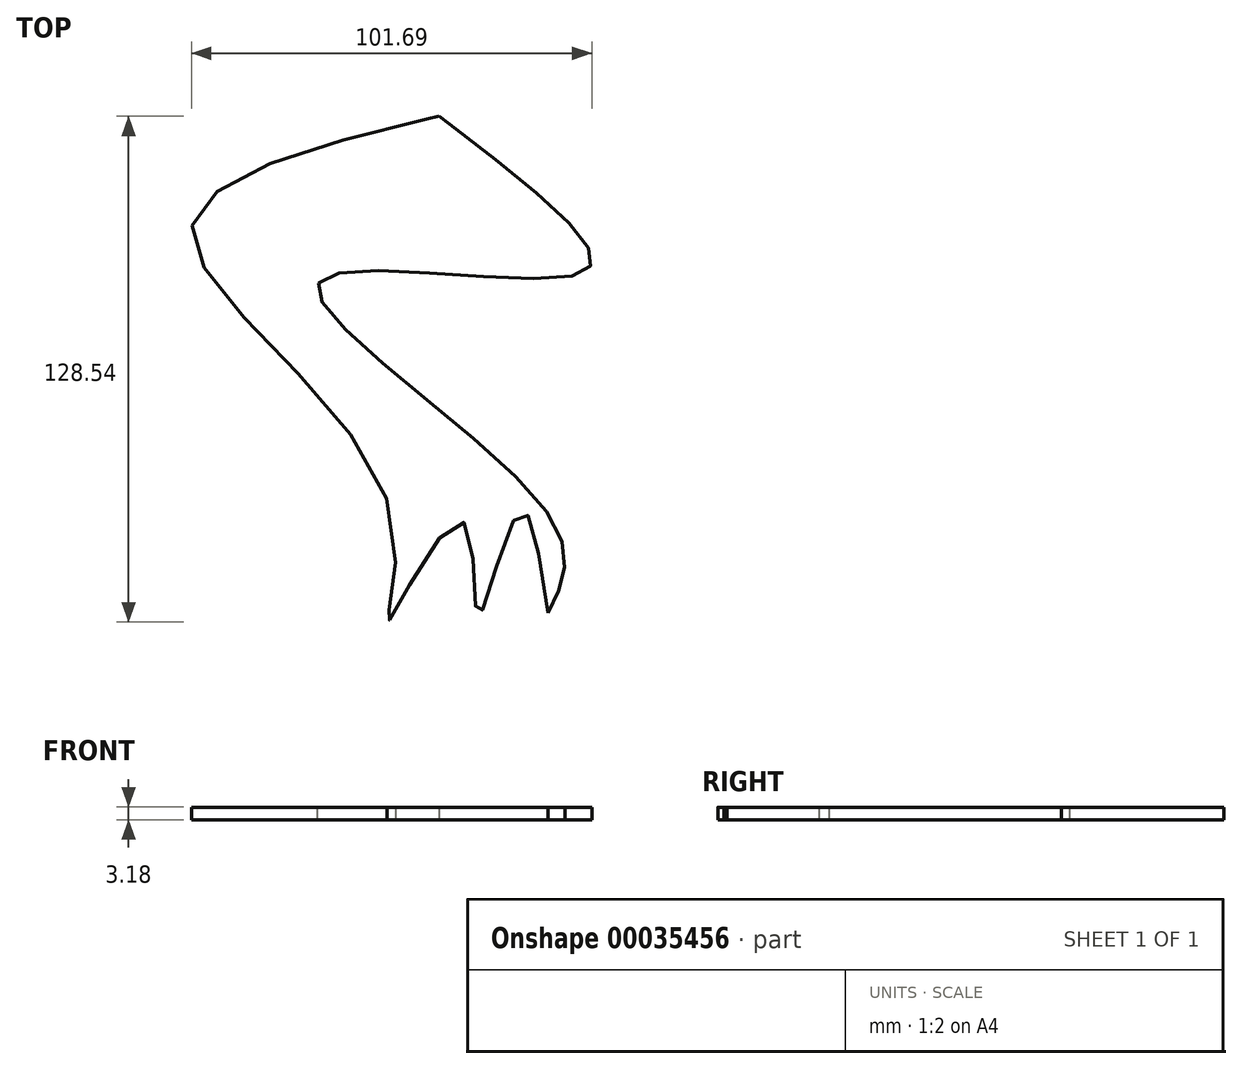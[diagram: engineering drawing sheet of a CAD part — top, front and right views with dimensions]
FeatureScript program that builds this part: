
annotation { "Feature Type Name" : "Feature", "Feature Type Description" : "" }
export const myFeature = defineFeature(function(context is Context, id is Id, definition is map)
    precondition{}
    {
        {
            var Q0;
            Q0=qCreatedBy(makeId("Top.planeOp"),FACE);
            var sketch = newSketch(context, id + "F0", { "sketchPlane" : qUnion([Q0])});
            skLineSegment(sketch, "E0", {"start": v(0, 123.85) * mm, "end": v(0, -125.19) * mm, "construction": true});
            skPoint(sketch, "E1.orphan", {"position": v(0, -125.19) * mm});
            skPoint(sketch, "E2.MirrorCS.end.orphan", {"position": v(0, 123.85) * mm});
            skFitSpline(sketch, "E3.MirrorCS", {"points": [v(-53.72, -66.97) * mm, v(-116.54, -97.18) * mm, v(-66.43, -165.92) * mm, v(-66.43, -195.15) * mm, v(-47.8, -169.87) * mm, v(-43.85, -193.97) * mm, v(-33.58, -167.9) * mm, v(-26.07, -193.18) * mm], "startDerivative": vector(-503.65, -120.96) * mm, "endDerivative": vector(51.87, -371.98) * mm});
            skFitSpline(sketch, "E4.MirrorCS", {"points": [v(-26.07, -193.18) * mm, v(-26.07, -167.9) * mm, v(-84.18, -109.1) * mm, v(-17.07, -106.69) * mm, v(-53.72, -66.97) * mm], "startDerivative": vector(66.51, 128.57) * mm, "endDerivative": vector(-279.5, 211.68) * mm});
            skFitSpline(sketch, "E5.MirrorCS", {"points": [v(-53.72, -66.97) * mm, v(-116.54, -97.18) * mm, v(-66.43, -165.92) * mm, v(-66.43, -195.15) * mm, v(-47.8, -169.87) * mm, v(-43.85, -193.97) * mm, v(-33.58, -167.9) * mm, v(-26.07, -193.18) * mm], "startDerivative": vector(-503.65, -120.96) * mm, "endDerivative": vector(51.87, -371.98) * mm});
            skArc(sketch, "E6.MirrorCS", {"start": v(-56.92, -67.74) * mm, "mid": v(-53.87, -67.7) * mm, "end": v(-51.1, -68.96) * mm});
            skSolve(sketch);
        }
        {
            var Q0;
            Q0=makeQuery(id+"F0.imprint","IMPRINT",FACE,{"disambiguationData":[TD([[makeQuery(id+"F0.imprint","IMPRINT",EDGE,{"derivedFrom":sQuery(id+"F0.wireOp",EDGE,"E4.MirrorCS")}),1.0]])]});
            extrude(context, id + "F1", {"entities" : qUnion([Q0]), "depth" : 3.17 * mm});
        }
    });
